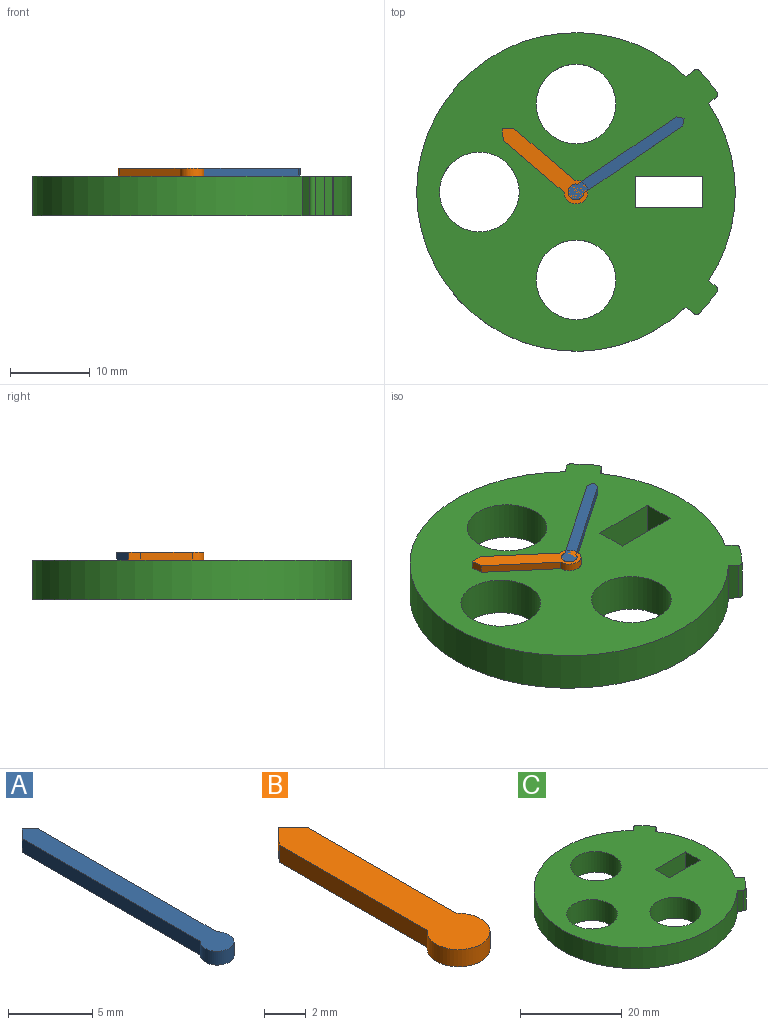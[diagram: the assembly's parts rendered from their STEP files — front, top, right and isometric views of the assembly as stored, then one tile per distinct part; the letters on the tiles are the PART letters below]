
ASSEMBLY  parts=3 mates=4
PART A: 7 faces, bbox 2x17.4x1 mm
  f0: plane 15x1mm, normal (-1,0,0), area 15mm2, adj f1,f4,f5,f6
  f1: cylinder r=1mm len=2mm, axis (0,0,-1), area 4.7mm2, adj f0,f2,f5,f6
  f2: plane 15x1mm, normal (1,0,0), area 15mm2, adj f1,f3,f5,f6
  f3: plane 1x0.7mm, normal (0.7,0.71,0), area 1mm2, adj f2,f4,f5,f6
  f4: plane 1x0.7mm, normal (-0.7,0.71,0), area 1mm2, adj f0,f3,f5,f6
  f5: plane 17.41x2mm, normal (0,0,1), area 24.4mm2, adj f0,f1,f2,f3,f4
  f6: plane 17.41x2mm, normal (0,0,-1), area 24.4mm2, adj f0,f1,f2,f3,f4
PART B: 7 faces, bbox 3x13.7x1 mm
  f0: plane 10x1mm, normal (-1,0,0), area 10mm2, adj f1,f4,f5,f6
  f1: cylinder r=1.5mm len=3mm, axis (0,0,-1), area 7.2mm2, adj f0,f2,f5,f6
  f2: plane 10x1mm, normal (1,0,0), area 10mm2, adj f1,f3,f5,f6
  f3: plane 1.08x1mm, normal (0.73,0.68,0), area 1.5mm2, adj f2,f4,f5,f6
  f4: plane 1.08x1mm, normal (-0.73,0.68,0), area 1.5mm2, adj f0,f3,f5,f6
  f5: plane 13.7x3mm, normal (0,0,1), area 27.6mm2, adj f0,f1,f2,f3,f4
  f6: plane 13.7x3mm, normal (0,0,-1), area 27.6mm2, adj f0,f1,f2,f3,f4
PART C: 23 faces, bbox 40x40x5 mm
  f0: plane 5x1.27mm, normal (0.74,0.67,0), area 8.6mm2, adj f1,f20,f21,f22
  f1: cylinder r=0.5mm len=5mm, axis (0,0,-1), area 3.8mm2, adj f0,f2,f21,f22
  f2: plane 5x0.96mm, normal (-0.64,0.77,0), area 6.3mm2, adj f1,f3,f21,f22
  f3: cylinder r=20mm len=40mm, axis (0,0,-1), area 466.7mm2, adj f2,f4,f21,f22
  f4: plane 5x0.96mm, normal (-0.64,-0.77,0), area 6.3mm2, adj f3,f5,f21,f22
  f5: cylinder r=0.5mm len=5mm, axis (0,0,-1), area 3.8mm2, adj f4,f6,f21,f22
  f6: plane 5x1.27mm, normal (0.74,-0.67,0), area 8.6mm2, adj f5,f7,f21,f22
  f7: plane 5x1.36mm, normal (0.79,-0.61,0), area 8.6mm2, adj f6,f8,f21,f22
  f8: cylinder r=0.5mm len=5mm, axis (0,0,-1), area 3.8mm2, adj f7,f9,f21,f22
  f9: plane 5x0.96mm, normal (0.65,0.76,0), area 6.3mm2, adj f8,f10,f21,f22
  f10: cylinder r=20mm len=22.19mm, axis (0,0,-1), area 117.6mm2, adj f9,f11,f21,f22
  f11: plane 5x0.96mm, normal (0.65,-0.76,0), area 6.3mm2, adj f10,f12,f21,f22
  f12: cylinder r=0.5mm len=5mm, axis (0,0,-1), area 3.8mm2, adj f11,f20,f21,f22
  f13: plane 5x4mm, normal (1,0,0), area 20mm2, adj f14,f19,f21,f22
  f14: plane 8.51x5mm, normal (0,-1,0), area 42.5mm2, adj f13,f15,f21,f22
  f15: plane 5x4mm, normal (-1,0,0), area 20mm2, adj f14,f19,f21,f22
  f16: cylinder r=5mm len=10mm, axis (0,0,-1), area 157.1mm2, adj f21,f22
  f17: cylinder r=5mm len=10mm, axis (0,0,-1), area 157.1mm2, adj f21,f22
  f18: cylinder r=5mm len=10mm, axis (0,0,-1), area 157.1mm2, adj f21,f22
  f19: plane 8.51x5mm, normal (0,1,0), area 42.5mm2, adj f13,f15,f21,f22
  f20: plane 5x1.36mm, normal (0.79,0.61,0), area 8.6mm2, adj f0,f12,f21,f22
  f21: plane 40x40mm, normal (0,0,1), area 1001.7mm2, adj f0,f1,f2,f3,f4,f5,f6,f7
  f22: plane 40x40mm, normal (0,0,-1), area 1001.7mm2, adj f0,f1,f2,f3,f4,f5,f6,f7
PLACE A rot(axis=(0,0,-1),55.7deg) t=(-2.38,-4.89,11.61)mm
PLACE B rot(axis=(0,0,1),49.5deg) t=(-2.38,-4.89,11.61)mm
PLACE C t=(-2.38,-4.89,6.61)mm fixed
MATE cylindrical C.f10 <-> A.f1  axis (0,0,-1) through (-2.38,-4.89,9.11)mm
MATE parallel A.f6 <-> C.f21  axis (0,0,-1) through (4.8,-0.84,11.61)mm
MATE cylindrical C.f10 <-> B.f1  axis (0,0,-1) through (-2.38,-4.89,9.11)mm
MATE parallel B.f6 <-> C.f21  axis (0,0,-1) through (-6.07,-1.74,11.61)mm
